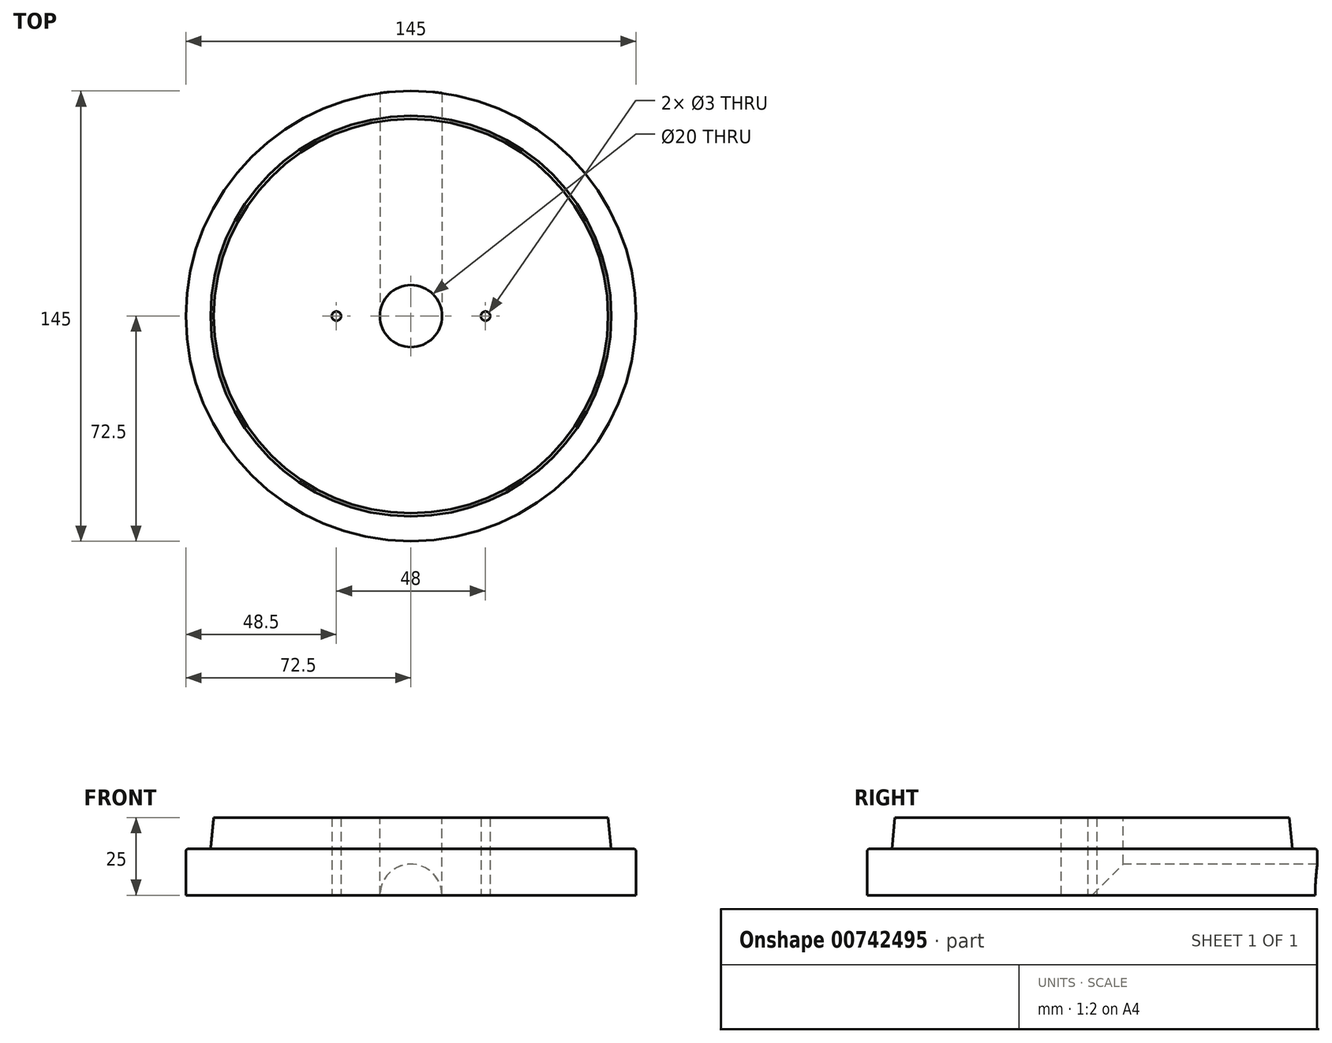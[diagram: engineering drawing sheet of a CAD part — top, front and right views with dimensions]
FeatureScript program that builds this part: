
annotation { "Feature Type Name" : "Feature", "Feature Type Description" : "" }
export const myFeature = defineFeature(function(context is Context, id is Id, definition is map)
    precondition{}
    {
        {
            var Q0;
            Q0=qCreatedBy(makeId("Front.planeOp"),FACE);
            var sketch = newSketch(context, id + "F0", { "sketchPlane" : qUnion([Q0])});
            skLineSegment(sketch, "E0", {"start": v(-72.5, 0) * mm, "end": v(72.5, 0) * mm});
            skLineSegment(sketch, "E1", {"start": v(72.5, 0) * mm, "end": v(72.5, 15) * mm});
            skLineSegment(sketch, "E2", {"start": v(72.5, 15) * mm, "end": v(64.5, 15) * mm});
            skLineSegment(sketch, "E3", {"start": v(64.5, 15) * mm, "end": v(64.5, 25) * mm});
            skLineSegment(sketch, "E4", {"start": v(64.5, 25) * mm, "end": v(-64.5, 25) * mm});
            skLineSegment(sketch, "E5", {"start": v(-64.5, 25) * mm, "end": v(-64.5, 15) * mm});
            skLineSegment(sketch, "E6", {"start": v(-64.5, 15) * mm, "end": v(-72.5, 15) * mm});
            skLineSegment(sketch, "E7", {"start": v(-72.5, 15) * mm, "end": v(-72.5, 0) * mm});
            skLineSegment(sketch, "E8", {"start": v(0, 0) * mm, "end": v(0, 25) * mm});
            skLineSegment(sketch, "E9", {"start": v(0, 25) * mm, "end": v(0, 43.04) * mm});
            skLineSegment(sketch, "E10", {"start": v(0, 43.04) * mm, "end": v(10, 43.04) * mm});
            skLineSegment(sketch, "E11", {"start": v(10, 43.04) * mm, "end": v(10, -6.96) * mm});
            skLineSegment(sketch, "E12", {"start": v(10, -6.96) * mm, "end": v(0, -6.96) * mm});
            skLineSegment(sketch, "E13", {"start": v(0, -6.96) * mm, "end": v(0, 43.04) * mm});
            skSolve(sketch);
        }
        {
            var Q0;
            {var subQ0=sQuery(id+"F0.wireOp",EDGE,"E5");Q0=makeQuery(id+"F0.imprint","IMPRINT",FACE,{"disambiguationData":[TD([[makeQuery(id+"F0.imprint","IMPRINT",EDGE,{"derivedFrom":subQ0}),1.0]])]});}
            var Q1;
            Q1=sQuery(id+"F0.wireOp",EDGE,"E8");
            revolve(context, id + "F1", {"surfaceOperationType" : NewSurfaceOperationType.NEW, "entities" : qUnion([Q0]), "axis" : qUnion([Q1]), "revolveType" : RevolveType.FULL});
        }
        {
            var Q0;
            {var subQ5=sQuery(id+"F0.wireOp",EDGE,"E10");Q0=makeQuery(id+"F0.imprint","IMPRINT",FACE,{"disambiguationData":[TD([[makeQuery(id+"F0.imprint","IMPRINT",EDGE,{"derivedFrom":subQ5}),-1.0]])]});}
            var Q1;
            {var subQ0=sQuery(id+"F0.wireOp",EDGE,"E13");var subQ1=sQuery(id+"F0.wireOp",EDGE,"E0");var subQ2=makeQuery(id+"F0.imprint","INTERSECT",VERTEX,{"derivedFrom":[subQ1,subQ0]});Q1=makeQuery(id+"F0.imprint","IMPRINT",FACE,{"disambiguationData":[TD([[makeQuery(id+"F0.imprint","IMPRINT",EDGE,{"disambiguationData":[TD([[subQ2,-1.0]])],"derivedFrom":subQ1}),1.0]])]});}
            var Q2;
            {var subQ5=sQuery(id+"F0.wireOp",EDGE,"E12");Q2=makeQuery(id+"F0.imprint","IMPRINT",FACE,{"disambiguationData":[TD([[makeQuery(id+"F0.imprint","IMPRINT",EDGE,{"derivedFrom":subQ5}),-1.0]])]});}
            var Q3;
            Q3=sQuery(id+"F0.wireOp",EDGE,"E13");
            revolve(context, id + "F2", {"operationType" : NewBodyOperationType.REMOVE, "surfaceOperationType" : NewSurfaceOperationType.NEW, "entities" : qUnion([Q0, Q1, Q2]), "axis" : qUnion([Q3]), "revolveType" : RevolveType.FULL, "oppositeDirection" : true});
        }
        {
            var Q0;
            Q0=qCreatedBy(makeId("Front.planeOp"),FACE);
            var sketch = newSketch(context, id + "F3", { "sketchPlane" : qUnion([Q0])});
            skCircle(sketch, "E14", {"center": v(0, 0) * mm, "radius": 10 * mm});
            skSolve(sketch);
        }
        {
            var Q0;
            Q0=makeQuery(id+"F3.imprint","IMPRINT",FACE,{"disambiguationData":[TD([[makeQuery(id+"F3.imprint","IMPRINT",EDGE,{"derivedFrom":sQuery(id+"F3.wireOp",EDGE,"E14")}),1.0]])]});
            extrude(context, id + "F4", {"entities" : qUnion([Q0]), "operationType" : NewBodyOperationType.REMOVE, "oppositeDirection" : true, "depth" : 141.6 * mm, "offsetDistance" : 25 * mm});
        }
        {
            var Q0;
            Q0=makeQuery(id+"F1.opRevolve","SWEPT_EDGE",EDGE,{"disambiguationData":[OSD([sQuery(id+"F0.wireOp",EDGE,"E6"),sQuery(id+"F0.wireOp",EDGE,"E7")])]});
            fillet(context, id + "F5", {"entities" : qUnion([Q0]), "radius" : 1 * mm, "tangentPropagation" : true, "allowEdgeOverflow" : false});
        }
        {
            var Q0;
            Q0=makeQuery(id+"F1.opRevolve","SWEPT_EDGE",EDGE,{"disambiguationData":[OSD([sQuery(id+"F0.wireOp",EDGE,"E4"),sQuery(id+"F0.wireOp",EDGE,"E5")])]});
            chamfer(context, id + "F6", {"entities" : qUnion([Q0]), "chamferType" : ChamferType.TWO_OFFSETS, "width1" : 10 * mm, "oppositeDirection" : false, "width2" : 1 * mm, "tangentPropagation" : true});
        }
        {
            var Q0;
            Q0=qCreatedBy(makeId("Top.planeOp"),FACE);
            var sketch = newSketch(context, id + "F7", { "sketchPlane" : qUnion([Q0])});
            skPoint(sketch, "E15", {"position": v(24, 0) * mm});
            skPoint(sketch, "E16", {"position": v(-24, 0) * mm});
            skSolve(sketch);
        }
        {
            var Q0;
            Q0=sQuery(id+"F7.wireOp",VERTEX,"E15");
            var Q1;
            Q1=makeQuery(id+"F1.opRevolve","SWEPT_BODY",BODY,{"disambiguationData":[OSD([sQuery(id+"F0.wireOp",EDGE,"E0"),sQuery(id+"F0.wireOp",EDGE,"E4"),sQuery(id+"F0.wireOp",EDGE,"E5"),sQuery(id+"F0.wireOp",EDGE,"E6"),sQuery(id+"F0.wireOp",EDGE,"E7"),sQuery(id+"F0.wireOp",EDGE,"E13")])]});
            hole(context, id + "F8", {"style" : HoleStyle.SIMPLE, "endStyle" : HoleEndStyle.THROUGH, "oppositeDirection" : true, "holeDiameter" : 3 * mm, "majorDiameter" : 5 * mm, "isTappedThrough" : true, "tappedDepth" : 12 * mm, "tapClearance" : 3, "locations" : qUnion([Q0]), "scope" : qUnion([Q1])});
        }
        {
            var Q0;
            Q0=sQuery(id+"F7.wireOp",VERTEX,"E16");
            var Q1;
            Q1=makeQuery(id+"F1.opRevolve","SWEPT_BODY",BODY,{"disambiguationData":[OSD([sQuery(id+"F0.wireOp",EDGE,"E0"),sQuery(id+"F0.wireOp",EDGE,"E4"),sQuery(id+"F0.wireOp",EDGE,"E5"),sQuery(id+"F0.wireOp",EDGE,"E6"),sQuery(id+"F0.wireOp",EDGE,"E7"),sQuery(id+"F0.wireOp",EDGE,"E13")])]});
            hole(context, id + "F9", {"style" : HoleStyle.SIMPLE, "endStyle" : HoleEndStyle.THROUGH, "oppositeDirection" : true, "holeDiameter" : 3 * mm, "majorDiameter" : 5 * mm, "isTappedThrough" : true, "tappedDepth" : 12 * mm, "tapClearance" : 3, "locations" : qUnion([Q0]), "scope" : qUnion([Q1])});
        }
    });
